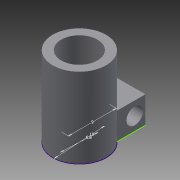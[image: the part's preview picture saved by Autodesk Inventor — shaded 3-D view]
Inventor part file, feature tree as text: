
AUTODESK INVENTOR PART (.ipt)
format: ipt  version: 2015 (Build 190159000, 159)  size: 115,712 bytes
history: native  units: in
note: dims shown in document units (in); Inventor stores cm internally (conversion verified against a paired STEP export)
features: extrude x5, sketch x3
ambient origin geometry x8: Origin, YZ Plane, XZ Plane, XY Plane, X Axis, Y Axis, Z Axis, Center Point
bodies: Solid1 (feature_tree)
feature tree (8):
  sketch  "Sketch1"  dims[d0=0.2677in d1=0.3937in]
  extrude  "Extrusion1"  Depth=0.3937in
  extrude  "Extrusion2"  Depth=0.1969in TaperAngle=0.0deg
  sketch  "Sketch2"  dims[d2=0.3543in d3=0.1969in d4=0.0in]
  extrude  "Extrusion3"  Depth=0.0984in
  extrude  "Extrusion4"  Depth=0.0787in
  extrude  "Extrusion5"  Depth=0.122in
  sketch  "Sketch3"  dims[d5=0.5906in d6=0.0in d7=0.0984in d8=0.0787in d9=0.122in d10=0.315in d11=0.5906in d12=0.0in d13=0.5906in d14=0.0in d15=0.0787in d16=0.0984in d17=0.315in d18=0.5906in d19=0.0in]
